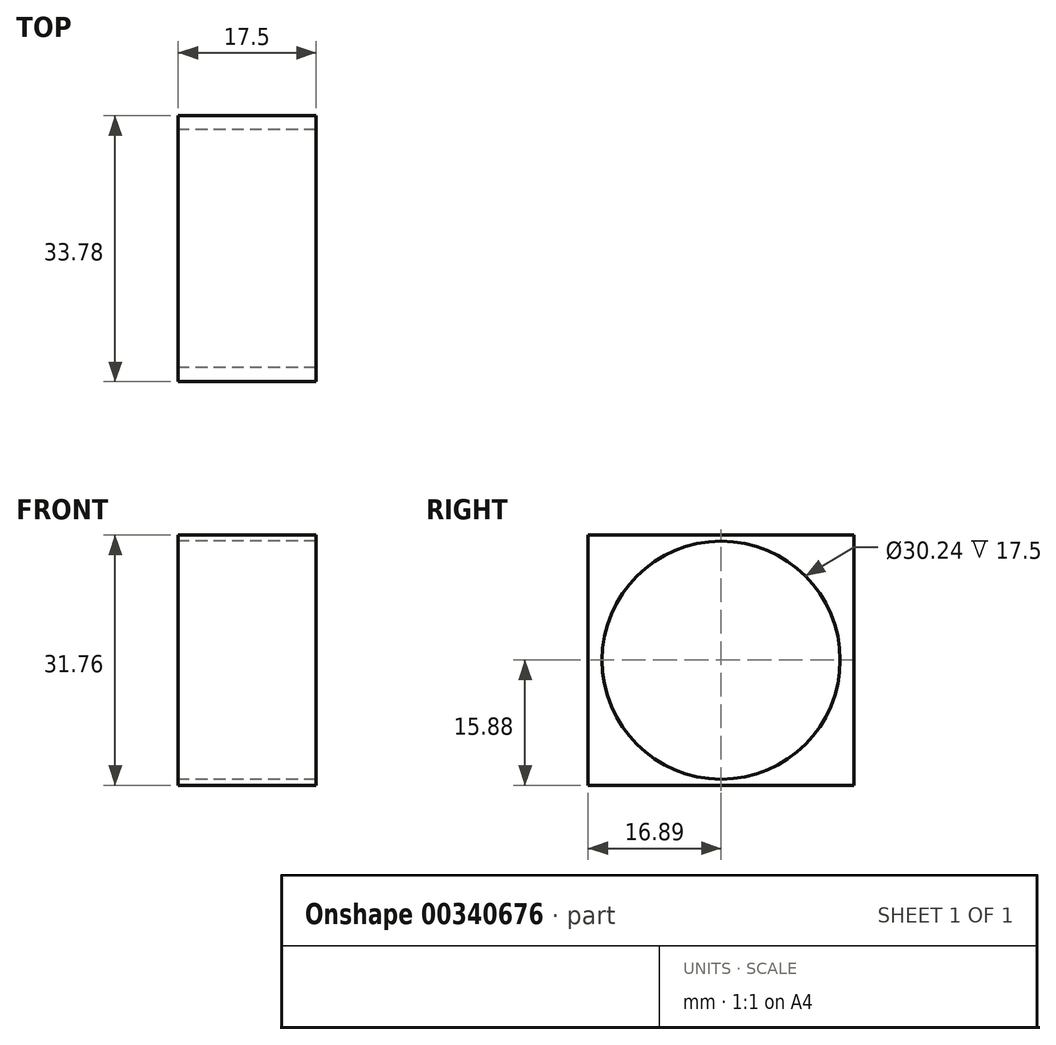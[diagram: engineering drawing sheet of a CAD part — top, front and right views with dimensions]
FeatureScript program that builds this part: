
annotation { "Feature Type Name" : "Feature", "Feature Type Description" : "" }
export const myFeature = defineFeature(function(context is Context, id is Id, definition is map)
    precondition{}
    {
        {
            var Q0;
            Q0=qCreatedBy(makeId("Right.planeOp"),FACE);
            var sketch = newSketch(context, id + "F0", { "sketchPlane" : qUnion([Q0])});
            skLineSegment(sketch, "E0.bottom", {"start": v(-16.88, 15.88) * mm, "end": v(16.88, 15.88) * mm});
            skLineSegment(sketch, "E0.top", {"start": v(-16.88, -15.88) * mm, "end": v(16.88, -15.88) * mm});
            skLineSegment(sketch, "E0.left", {"start": v(-16.89, 15.88) * mm, "end": v(-16.89, -15.88) * mm});
            skLineSegment(sketch, "E0.right", {"start": v(16.88, 15.88) * mm, "end": v(16.88, -15.88) * mm});
            skPoint(sketch, "E0.middle", {"position": v(0, 0) * mm});
            skCircle(sketch, "E1", {"center": v(0, 0) * mm, "radius": 15.12 * mm});
            skSolve(sketch);
        }
        {
            var Q0;
            Q0 = qSketchRegion(id + "F0", true);
            extrude(context, id + "F1", {"entities" : qUnion([Q0]), "depth" : 17.5 * mm});
        }
    });
